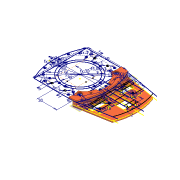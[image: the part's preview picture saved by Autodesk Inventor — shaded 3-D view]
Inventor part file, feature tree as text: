
AUTODESK INVENTOR PART (.ipt)
format: ipt  version: 2020.3 (Build 243373000, 373)  size: 276,992 bytes
history: native  units: mm
features: extrude x4, sketch x2, fillet x2, plane x1
ambient origin geometry x8: Origin, YZ Plane, XZ Plane, XY Plane, X Axis, Y Axis, Z Axis, Center Point
bodies: Solid1 (feature_tree)
feature tree (9):
  sketch  "Sketch1"  dims[d1=40.0mm d3=20.0mm d5=200.0mm d6=60.0mm d7=81.0mm d8=3.0mm d9=7.5mm d10=5.0mm d11=30.0mm d12=3.0mm d13=7.5mm d14=5.0mm d15=3.0mm d16=3.0mm d17=5.0mm d18=48.0mm d19=55.0mm d20=3.0mm d21=4.5mm d22=3.0mm d23=4.5mm d24=360.0deg d25=80.0mm d26=72.56mm d27=3.0mm d28=3.0mm d29=360.0deg d30=45.0deg d31=3.0mm d32=360.0deg d33=3.0mm d34=3.0mm d35=3.0mm d36=3.0mm d37=6.0mm]
  extrude  "Extrusion1"  Depth=6.0mm
  extrude  "Extrusion2"  Depth=15.0mm
  plane  "Work Plane1"
  sketch  "Sketch2"  dims[d38=5.0mm d39=30.0mm d40=40.5mm d41=14.0mm d42=18.0mm d43=19.0mm d44=14.0mm d45=7.0mm d46=2.0mm d47=2.0mm d48=2.0mm d49=2.0mm d50=2.0mm d51=2.0mm d52=7.0mm d53=2.5mm d54=2.5mm d55=2.0mm d56=2.0mm d57=2.5mm d58=2.0mm d59=2.0mm d60=35.0mm d61=16.0mm d62=4.0mm d63=4.0mm d64=22.0mm d65=14.0mm d66=13.962634mm d67=13.962634mm d68=2.0mm d69=4.0mm d70=2.0mm d71=0.0mm d72=4.0mm d73=0.0mm d74=1.5mm d75=2.5mm d76=0.0mm d77=2.0mm d78=6.5mm d79=6.5mm d80=1.25mm d81=0.0mm d82=15.0mm d83=0.872665mm]
  extrude  "Extrusion3"  Depth=15.0mm
  extrude  "Extrusion4"  Depth=15.0mm
  fillet  "Fillet1"  Radius=18.0mm
  fillet  "Fillet2"  Radius=19.0mm
